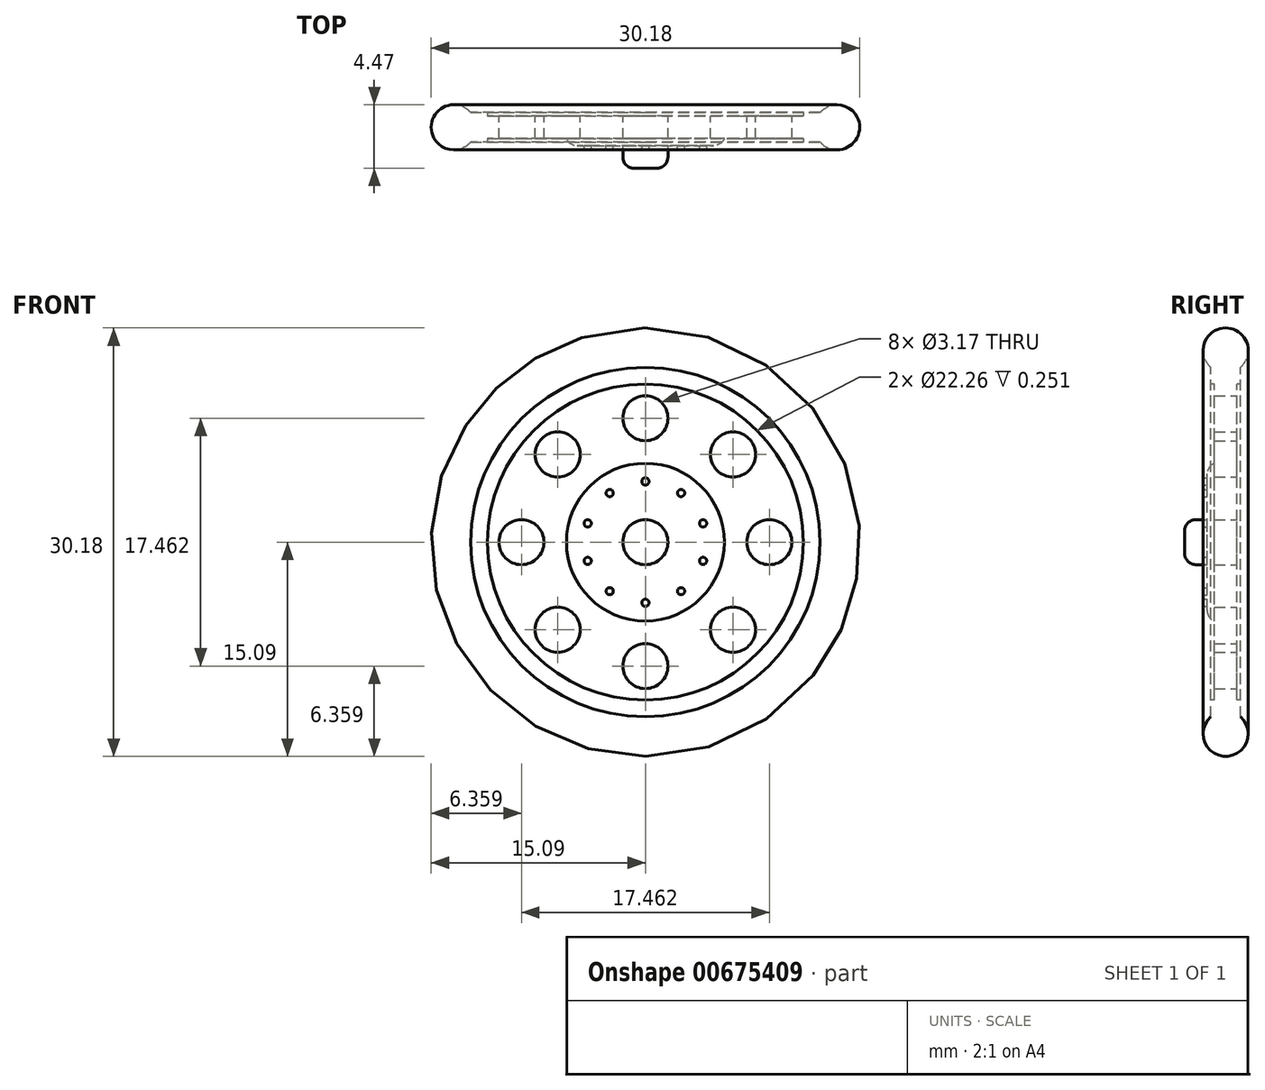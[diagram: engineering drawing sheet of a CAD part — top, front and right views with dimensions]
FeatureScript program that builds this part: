
annotation { "Feature Type Name" : "Feature", "Feature Type Description" : "" }
export const myFeature = defineFeature(function(context is Context, id is Id, definition is map)
    precondition{}
    {
        {
            var Q0;
            Q0=qCreatedBy(makeId("Front.planeOp"),FACE);
            var sketch = newSketch(context, id + "F0", { "sketchPlane" : qUnion([Q0])});
            skCircle(sketch, "E0", {"center": v(0, 0) * mm, "radius": 11.9 * mm});
            skCircle(sketch, "E1", {"center": v(0, 0) * mm, "radius": 5.56 * mm});
            skCircle(sketch, "E2", {"center": v(0, 8.73) * mm, "radius": 1.59 * mm});
            skCircle(sketch, "E3.1.0", {"center": v(-6.17, 6.17) * mm, "radius": 1.59 * mm});
            skCircle(sketch, "E3.2.0", {"center": v(-8.73, 0) * mm, "radius": 1.59 * mm});
            skCircle(sketch, "E3.3.0", {"center": v(-6.17, -6.17) * mm, "radius": 1.59 * mm});
            skCircle(sketch, "E3.4.0", {"center": v(0, -8.73) * mm, "radius": 1.59 * mm});
            skCircle(sketch, "E3.5.0", {"center": v(6.17, -6.17) * mm, "radius": 1.59 * mm});
            skCircle(sketch, "E3.6.0", {"center": v(8.73, 0) * mm, "radius": 1.59 * mm});
            skCircle(sketch, "E3.7.0", {"center": v(6.17, 6.17) * mm, "radius": 1.59 * mm});
            skSolve(sketch);
        }
        {
            var Q0;
            Q0=makeQuery(id+"F0.imprint","IMPRINT",FACE,{"disambiguationData":[TD([[makeQuery(id+"F0.imprint","IMPRINT",EDGE,{"derivedFrom":sQuery(id+"F0.wireOp",EDGE,"E1")}),1.0]])]});
            var Q1;
            Q1=makeQuery(id+"F0.imprint","IMPRINT",FACE,{"disambiguationData":[TD([[makeQuery(id+"F0.imprint","IMPRINT",EDGE,{"derivedFrom":sQuery(id+"F0.wireOp",EDGE,"E0")}),1.0]])]});
            extrude(context, id + "F1", {"entities" : qUnion([Q0, Q1]), "depth" : 1.59 * mm, "offsetDistance" : 25.4 * mm});
        }
        {
            var Q0;
            Q0=makeQuery(id+"F1.opExtrude","CAP_FACE",FACE,{"disambiguationData":[OSD([sQuery(id+"F0.wireOp",EDGE,"E0"),sQuery(id+"F0.wireOp",EDGE,"E2"),sQuery(id+"F0.wireOp",EDGE,"E3.1.0"),sQuery(id+"F0.wireOp",EDGE,"E3.2.0"),sQuery(id+"F0.wireOp",EDGE,"E3.3.0"),sQuery(id+"F0.wireOp",EDGE,"E3.4.0"),sQuery(id+"F0.wireOp",EDGE,"E3.5.0"),sQuery(id+"F0.wireOp",EDGE,"E3.6.0"),sQuery(id+"F0.wireOp",EDGE,"E3.7.0")])],"isStart":false});
            var sketch = newSketch(context, id + "F2", { "sketchPlane" : qUnion([Q0])});
            skCircle(sketch, "E4", {"center": v(0, 0) * mm, "radius": 5.56 * mm});
            skSolve(sketch);
        }
        {
            var Q0;
            Q0=makeQuery(id+"F2.imprint","IMPRINT",FACE,{"disambiguationData":[TD([[makeQuery(id+"F2.imprint","IMPRINT",EDGE,{"derivedFrom":sQuery(id+"F2.wireOp",EDGE,"E4")}),1.0]])]});
            extrude(context, id + "F3", {"entities" : qUnion([Q0]), "operationType" : NewBodyOperationType.ADD, "depth" : 0.5 * mm, "offsetDistance" : 25.4 * mm});
        }
        {
            var Q0;
            Q0=makeQuery(id+"F3.opExtrude","CAP_FACE",FACE,{"disambiguationData":[OSD([sQuery(id+"F2.wireOp",EDGE,"E4")])],"isStart":false});
            var sketch = newSketch(context, id + "F4", { "sketchPlane" : qUnion([Q0])});
            skCircle(sketch, "E5", {"center": v(0, 4.27) * mm, "radius": 0.25 * mm});
            skCircle(sketch, "E6.1.0", {"center": v(-2.51, 3.46) * mm, "radius": 0.25 * mm});
            skCircle(sketch, "E6.2.0", {"center": v(-4.06, 1.32) * mm, "radius": 0.25 * mm});
            skCircle(sketch, "E6.3.0", {"center": v(-4.06, -1.32) * mm, "radius": 0.25 * mm});
            skCircle(sketch, "E6.4.0", {"center": v(-2.51, -3.46) * mm, "radius": 0.25 * mm});
            skCircle(sketch, "E6.5.0", {"center": v(0, -4.27) * mm, "radius": 0.25 * mm});
            skCircle(sketch, "E6.6.0", {"center": v(2.51, -3.46) * mm, "radius": 0.25 * mm});
            skCircle(sketch, "E6.7.0", {"center": v(4.06, -1.32) * mm, "radius": 0.25 * mm});
            skCircle(sketch, "E6.8.0", {"center": v(4.06, 1.32) * mm, "radius": 0.25 * mm});
            skCircle(sketch, "E6.9.0", {"center": v(2.51, 3.46) * mm, "radius": 0.25 * mm});
            skPoint(sketch, "E6.center", {"position": v(0, 0) * mm});
            skSolve(sketch);
        }
        {
            var Q0;
            Q0=makeQuery(id+"F4.imprint","IMPRINT",FACE,{"disambiguationData":[TD([[makeQuery(id+"F4.imprint","IMPRINT",EDGE,{"derivedFrom":sQuery(id+"F4.wireOp",EDGE,"E6.1.0")}),1.0]])]});
            var Q1;
            Q1=makeQuery(id+"F4.imprint","IMPRINT",FACE,{"disambiguationData":[TD([[makeQuery(id+"F4.imprint","IMPRINT",EDGE,{"derivedFrom":sQuery(id+"F4.wireOp",EDGE,"E5")}),1.0]])]});
            var Q2;
            Q2=makeQuery(id+"F4.imprint","IMPRINT",FACE,{"disambiguationData":[TD([[makeQuery(id+"F4.imprint","IMPRINT",EDGE,{"derivedFrom":sQuery(id+"F4.wireOp",EDGE,"E6.9.0")}),1.0]])]});
            var Q3;
            Q3=makeQuery(id+"F4.imprint","IMPRINT",FACE,{"disambiguationData":[TD([[makeQuery(id+"F4.imprint","IMPRINT",EDGE,{"derivedFrom":sQuery(id+"F4.wireOp",EDGE,"E6.8.0")}),1.0]])]});
            var Q4;
            Q4=makeQuery(id+"F4.imprint","IMPRINT",FACE,{"disambiguationData":[TD([[makeQuery(id+"F4.imprint","IMPRINT",EDGE,{"derivedFrom":sQuery(id+"F4.wireOp",EDGE,"E6.7.0")}),1.0]])]});
            var Q5;
            Q5=makeQuery(id+"F4.imprint","IMPRINT",FACE,{"disambiguationData":[TD([[makeQuery(id+"F4.imprint","IMPRINT",EDGE,{"derivedFrom":sQuery(id+"F4.wireOp",EDGE,"E6.6.0")}),1.0]])]});
            var Q6;
            Q6=makeQuery(id+"F4.imprint","IMPRINT",FACE,{"disambiguationData":[TD([[makeQuery(id+"F4.imprint","IMPRINT",EDGE,{"derivedFrom":sQuery(id+"F4.wireOp",EDGE,"E6.5.0")}),1.0]])]});
            var Q7;
            Q7=makeQuery(id+"F4.imprint","IMPRINT",FACE,{"disambiguationData":[TD([[makeQuery(id+"F4.imprint","IMPRINT",EDGE,{"derivedFrom":sQuery(id+"F4.wireOp",EDGE,"E6.4.0")}),1.0]])]});
            var Q8;
            Q8=makeQuery(id+"F4.imprint","IMPRINT",FACE,{"disambiguationData":[TD([[makeQuery(id+"F4.imprint","IMPRINT",EDGE,{"derivedFrom":sQuery(id+"F4.wireOp",EDGE,"E6.3.0")}),1.0]])]});
            var Q9;
            Q9=makeQuery(id+"F4.imprint","IMPRINT",FACE,{"disambiguationData":[TD([[makeQuery(id+"F4.imprint","IMPRINT",EDGE,{"derivedFrom":sQuery(id+"F4.wireOp",EDGE,"E6.2.0")}),1.0]])]});
            extrude(context, id + "F5", {"entities" : qUnion([Q0, Q1, Q2, Q3, Q4, Q5, Q6, Q7, Q8, Q9]), "operationType" : NewBodyOperationType.ADD, "depth" : 0.25 * mm, "offsetDistance" : 25.4 * mm});
        }
        {
            var Q0;
            Q0=makeQuery(id+"F3.opExtrude","CAP_FACE",FACE,{"disambiguationData":[OSD([sQuery(id+"F2.wireOp",EDGE,"E4")])],"isStart":false});
            var sketch = newSketch(context, id + "F6", { "sketchPlane" : qUnion([Q0])});
            skCircle(sketch, "E7", {"center": v(0, 0) * mm, "radius": 1.59 * mm});
            skSolve(sketch);
        }
        {
            var Q0;
            Q0=makeQuery(id+"F6.imprint","IMPRINT",FACE,{"disambiguationData":[TD([[makeQuery(id+"F6.imprint","IMPRINT",EDGE,{"derivedFrom":sQuery(id+"F6.wireOp",EDGE,"E7")}),1.0]])]});
            extrude(context, id + "F7", {"entities" : qUnion([Q0]), "operationType" : NewBodyOperationType.ADD, "depth" : 1.59 * mm, "offsetDistance" : 25.4 * mm});
        }
        {
            var Q0;
            Q0=makeQuery(id+"F7.opExtrude","CAP_EDGE",EDGE,{"disambiguationData":[OSD([sQuery(id+"F6.wireOp",EDGE,"E7")])],"isStart":false});
            var Q1;
            Q1=makeQuery(id+"F7.opExtrude","CAP_EDGE",EDGE,{"disambiguationData":[OSD([sQuery(id+"F6.wireOp",EDGE,"E7")])],"isStart":true});
            var Q2;
            Q2=makeQuery(id+"F3.opExtrude","CAP_EDGE",EDGE,{"disambiguationData":[OSD([sQuery(id+"F2.wireOp",EDGE,"E4")])],"isStart":false});
            fillet(context, id + "F8", {"entities" : qUnion([Q0, Q1, Q2]), "radius" : 0.8 * mm, "allowEdgeOverflow" : false});
        }
        {
            var Q0;
            Q0=qCreatedBy(makeId("Right.planeOp"),FACE);
            var sketch = newSketch(context, id + "F9", { "sketchPlane" : qUnion([Q0])});
            skLineSegment(sketch, "E8", {"start": v(0, 7.14) * mm, "end": v(-1.59, 7.14) * mm});
            skLineSegment(sketch, "E9", {"start": v(-1.59, 10.32) * mm, "end": v(0, 10.32) * mm});
            skArc(sketch, "E10", {"start": v(0.25, 12.3) * mm, "mid": v(-0.8, 15.1) * mm, "end": v(-1.84, 12.3) * mm});
            skLineSegment(sketch, "E11", {"start": v(-1.84, 12.3) * mm, "end": v(-1.84, 11.13) * mm});
            skLineSegment(sketch, "E12", {"start": v(-1.84, 11.13) * mm, "end": v(0.25, 11.13) * mm});
            skLineSegment(sketch, "E13", {"start": v(0.25, 11.13) * mm, "end": v(0.25, 12.3) * mm});
            skLineSegment(sketch, "E14", {"start": v(-5.73, 0) * mm, "end": v(3.05, 0) * mm});
            skSolve(sketch);
        }
        {
            var Q0;
            Q0=makeQuery(id+"F9.imprint","IMPRINT",FACE,{"disambiguationData":[TD([[makeQuery(id+"F9.imprint","IMPRINT",EDGE,{"derivedFrom":sQuery(id+"F9.wireOp",EDGE,"E10")}),1.0]])]});
            var Q1;
            Q1=sQuery(id+"F9.wireOp",EDGE,"E14");
            revolve(context, id + "F10", {"operationType" : NewBodyOperationType.ADD, "entities" : qUnion([Q0]), "axis" : qUnion([Q1]), "revolveType" : RevolveType.FULL});
        }
    });
